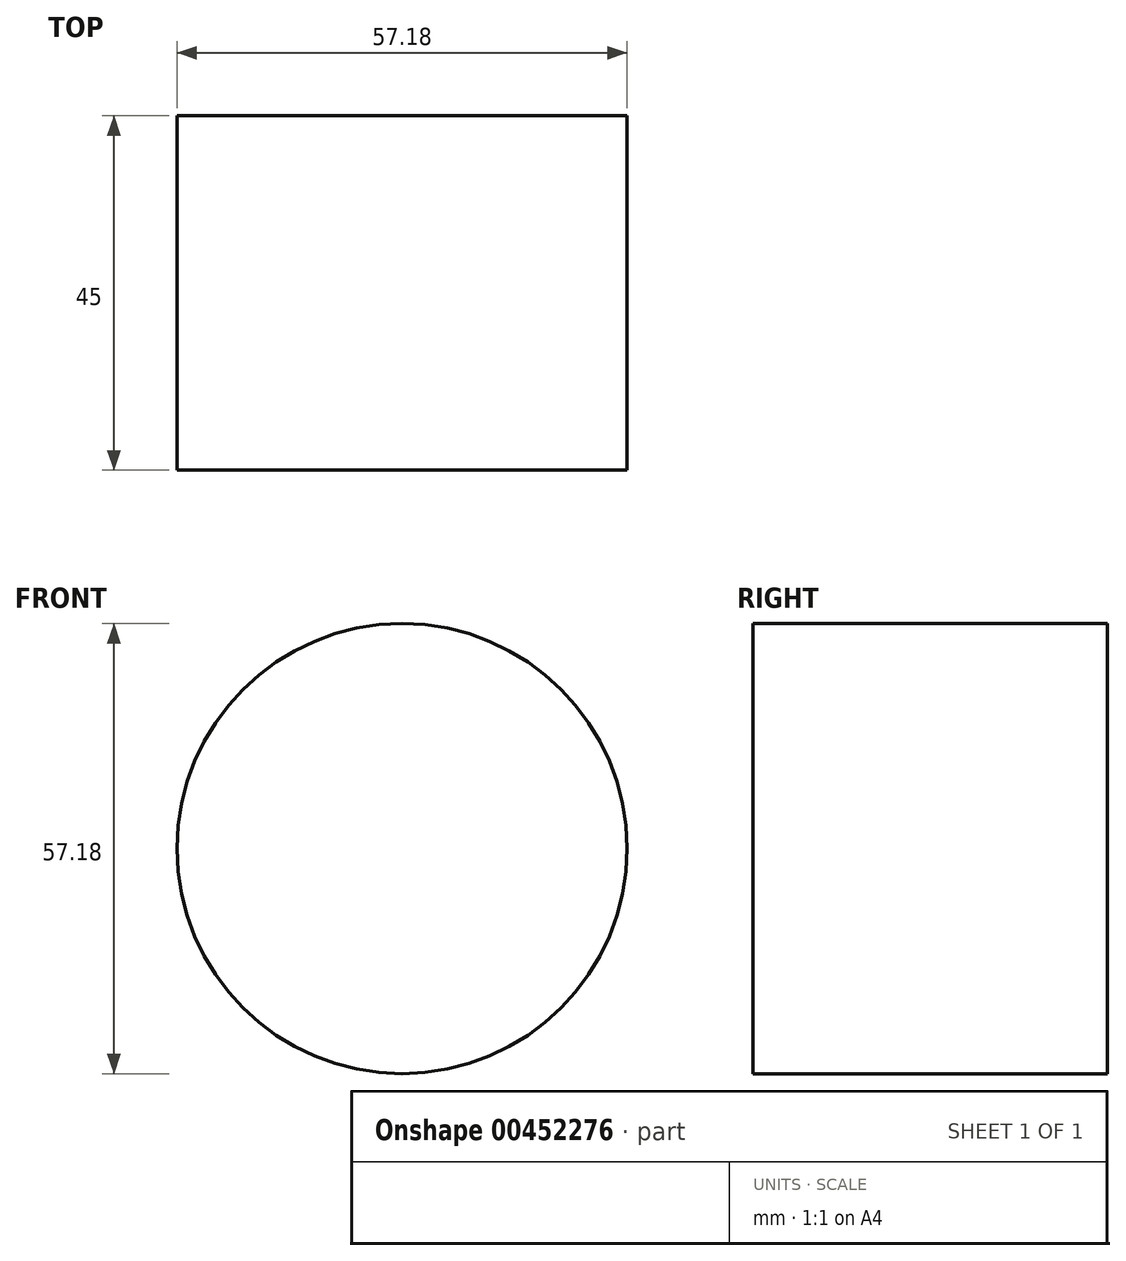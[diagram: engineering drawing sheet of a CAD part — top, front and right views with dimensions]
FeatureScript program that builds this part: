
annotation { "Feature Type Name" : "Feature", "Feature Type Description" : "" }
export const myFeature = defineFeature(function(context is Context, id is Id, definition is map)
    precondition{}
    {
        {
            var Q0;
            Q0=qCreatedBy(makeId("Front.planeOp"),FACE);
            var sketch = newSketch(context, id + "F0", { "sketchPlane" : qUnion([Q0])});
            skCircle(sketch, "E0", {"center": v(0, 0) * mm, "radius": 28.59 * mm});
            skSolve(sketch);
        }
        {
            var Q0;
            Q0=qSketchRegion(id+"F0",true);
            extrude(context, id + "F1", {"entities" : qUnion([Q0]), "depth" : 45 * mm, "offsetDistance" : 25 * mm});
        }
    });
